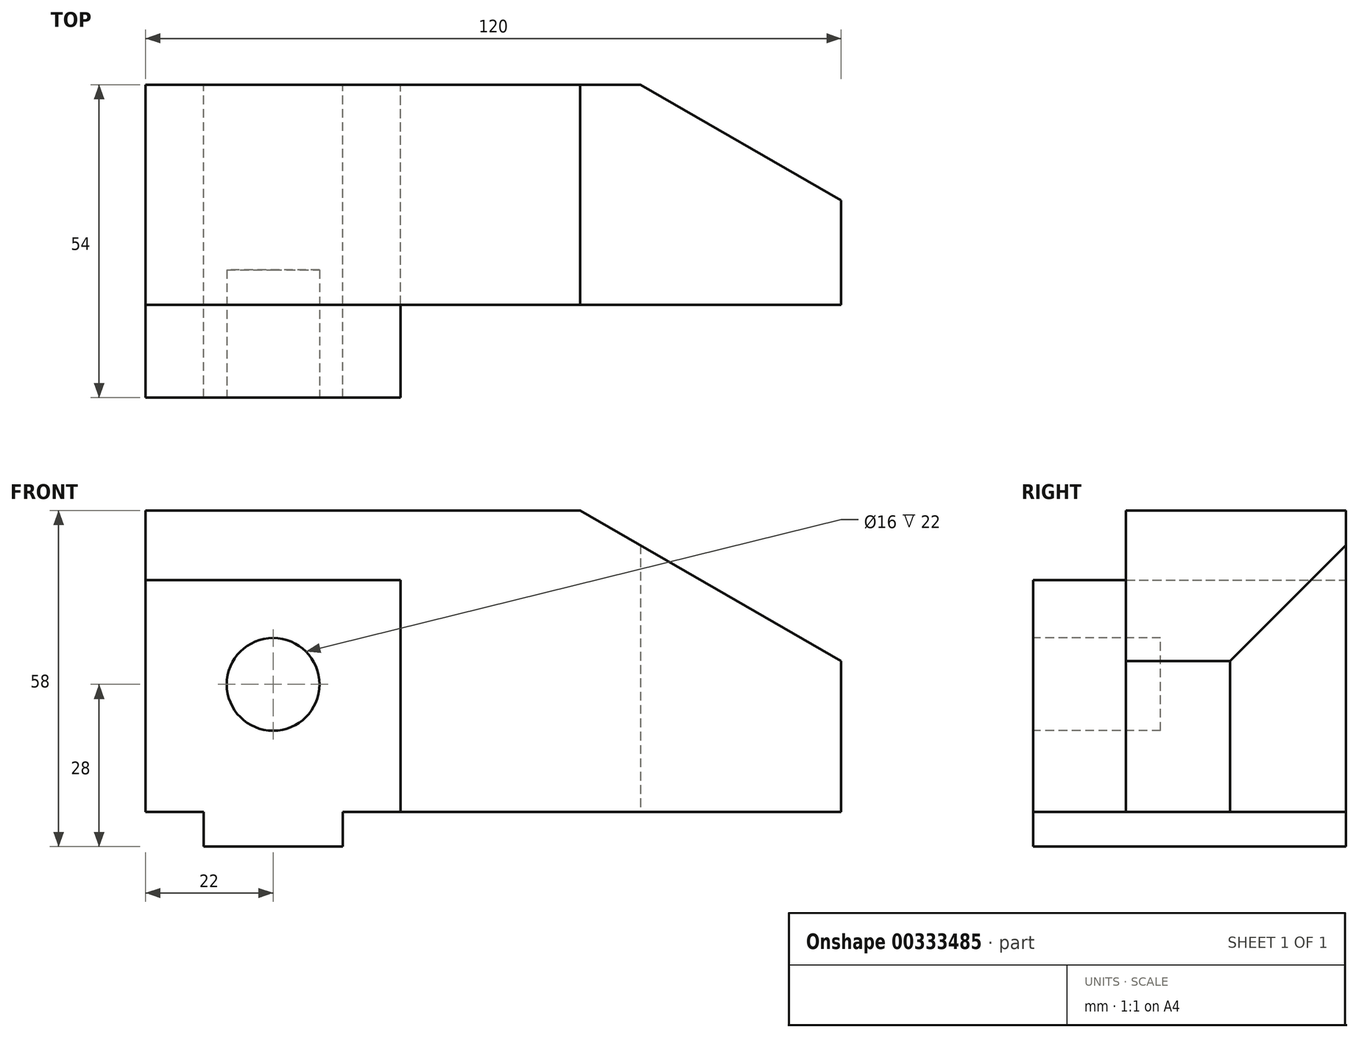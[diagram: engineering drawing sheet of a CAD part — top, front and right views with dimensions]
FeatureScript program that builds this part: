
annotation { "Feature Type Name" : "Feature", "Feature Type Description" : "" }
export const myFeature = defineFeature(function(context is Context, id is Id, definition is map)
    precondition{}
    {
        {
            var Q0;
            Q0=qCreatedBy(makeId("Front.planeOp"),FACE);
            var sketch = newSketch(context, id + "F0", { "sketchPlane" : qUnion([Q0])});
            skLineSegment(sketch, "E0", {"start": v(0, 0) * mm, "end": v(0, 52) * mm});
            skLineSegment(sketch, "E1", {"start": v(0, 52) * mm, "end": v(75, 52) * mm});
            skLineSegment(sketch, "E2", {"start": v(75, 52) * mm, "end": v(120, 26.02) * mm});
            skLineSegment(sketch, "E3", {"start": v(120, 26.02) * mm, "end": v(120, 0) * mm});
            skLineSegment(sketch, "E4", {"start": v(75, 52) * mm, "end": v(75, 0) * mm});
            skLineSegment(sketch, "E5", {"start": v(0, 40) * mm, "end": v(44, 40) * mm});
            skLineSegment(sketch, "E6", {"start": v(44, 40) * mm, "end": v(44, 0) * mm});
            skLineSegment(sketch, "E7", {"start": v(44, 0) * mm, "end": v(34, 0) * mm});
            skLineSegment(sketch, "E8", {"start": v(34, 0) * mm, "end": v(34, -6) * mm});
            skLineSegment(sketch, "E9", {"start": v(34, -6) * mm, "end": v(10, -6) * mm});
            skLineSegment(sketch, "E10", {"start": v(10, -6) * mm, "end": v(10, 0) * mm});
            skLineSegment(sketch, "E11", {"start": v(10, 0) * mm, "end": v(0, 0) * mm});
            skLineSegment(sketch, "E12", {"start": v(0, 0) * mm, "end": v(0, 40) * mm});
            skPoint(sketch, "E13.centerSnap0", {"position": v(44, 20) * mm});
            skCircle(sketch, "E14", {"center": v(22, 22) * mm, "radius": 8 * mm});
            skLineSegment(sketch, "E15", {"start": v(120, 0) * mm, "end": v(44, 0) * mm});
            skSolve(sketch);
        }
        {
            var Q0;
            Q0=makeQuery(id+"F0.imprint","IMPRINT",FACE,{"disambiguationData":[TD([[makeQuery(id+"F0.imprint","IMPRINT",EDGE,{"derivedFrom":sQuery(id+"F0.wireOp",EDGE,"E2")}),-1.0]])]});
            var Q1;
            Q1=makeQuery(id+"F0.imprint","IMPRINT",FACE,{"disambiguationData":[TD([[makeQuery(id+"F0.imprint","IMPRINT",EDGE,{"derivedFrom":sQuery(id+"F0.wireOp",EDGE,"E0")}),-1.0]])]});
            extrude(context, id + "F1", {"entities" : qUnion([Q0, Q1]), "depth" : 38 * mm});
        }
        {
            var Q0;
            Q0=makeQuery(id+"F0.imprint","IMPRINT",FACE,{"disambiguationData":[TD([[makeQuery(id+"F0.imprint","IMPRINT",EDGE,{"derivedFrom":sQuery(id+"F0.wireOp",EDGE,"E5")}),-1.0]])]});
            var Q1;
            Q1=makeQuery(id+"F0.imprint","IMPRINT",FACE,{"disambiguationData":[TD([[makeQuery(id+"F0.imprint","IMPRINT",EDGE,{"derivedFrom":sQuery(id+"F0.wireOp",EDGE,"E14")}),1.0]])]});
            extrude(context, id + "F2", {"entities" : qUnion([Q0, Q1]), "depth" : 54 * mm});
        }
        {
            var Q0;
            Q0=makeQuery(id+"F1.opExtrude","SWEPT_FACE",FACE,{"disambiguationData":[OSD([sQuery(id+"F0.wireOp",EDGE,"E15")])]});
            var sketch = newSketch(context, id + "F3", { "sketchPlane" : qUnion([Q0])});
            skLineSegment(sketch, "E16", {"start": v(120, 0) * mm, "end": v(85.36, 0) * mm});
            skLineSegment(sketch, "E17", {"start": v(85.36, 0) * mm, "end": v(120, 20) * mm});
            skLineSegment(sketch, "E18", {"start": v(120, 20) * mm, "end": v(120, 0) * mm});
            skSolve(sketch);
        }
        {
            var Q0;
            Q0 = qSketchRegion(id + "F3", true);
            extrude(context, id + "F4", {"entities" : qUnion([Q0]), "operationType" : NewBodyOperationType.REMOVE, "endBound" : BoundingType.THROUGH_ALL, "oppositeDirection" : true, "depth" : 25 * mm});
        }
        {
            var Q0;
            Q0=makeQuery(id+"F2.opExtrude","CAP_FACE",FACE,{"disambiguationData":[OSD([sQuery(id+"F0.wireOp",EDGE,"E5"),sQuery(id+"F0.wireOp",EDGE,"E6"),sQuery(id+"F0.wireOp",EDGE,"E7"),sQuery(id+"F0.wireOp",EDGE,"E8"),sQuery(id+"F0.wireOp",EDGE,"E9"),sQuery(id+"F0.wireOp",EDGE,"E10"),sQuery(id+"F0.wireOp",EDGE,"E11"),sQuery(id+"F0.wireOp",EDGE,"E12")])],"isStart":false});
            var sketch = newSketch(context, id + "F5", { "sketchPlane" : qUnion([Q0])});
            skCircle(sketch, "E19", {"center": v(22, 22) * mm, "radius": 8 * mm});
            skSolve(sketch);
        }
        {
            var Q0;
            Q0 = qSketchRegion(id + "F5", true);
            extrude(context, id + "F6", {"entities" : qUnion([Q0]), "operationType" : NewBodyOperationType.REMOVE, "oppositeDirection" : true, "depth" : 22 * mm});
        }
    });
